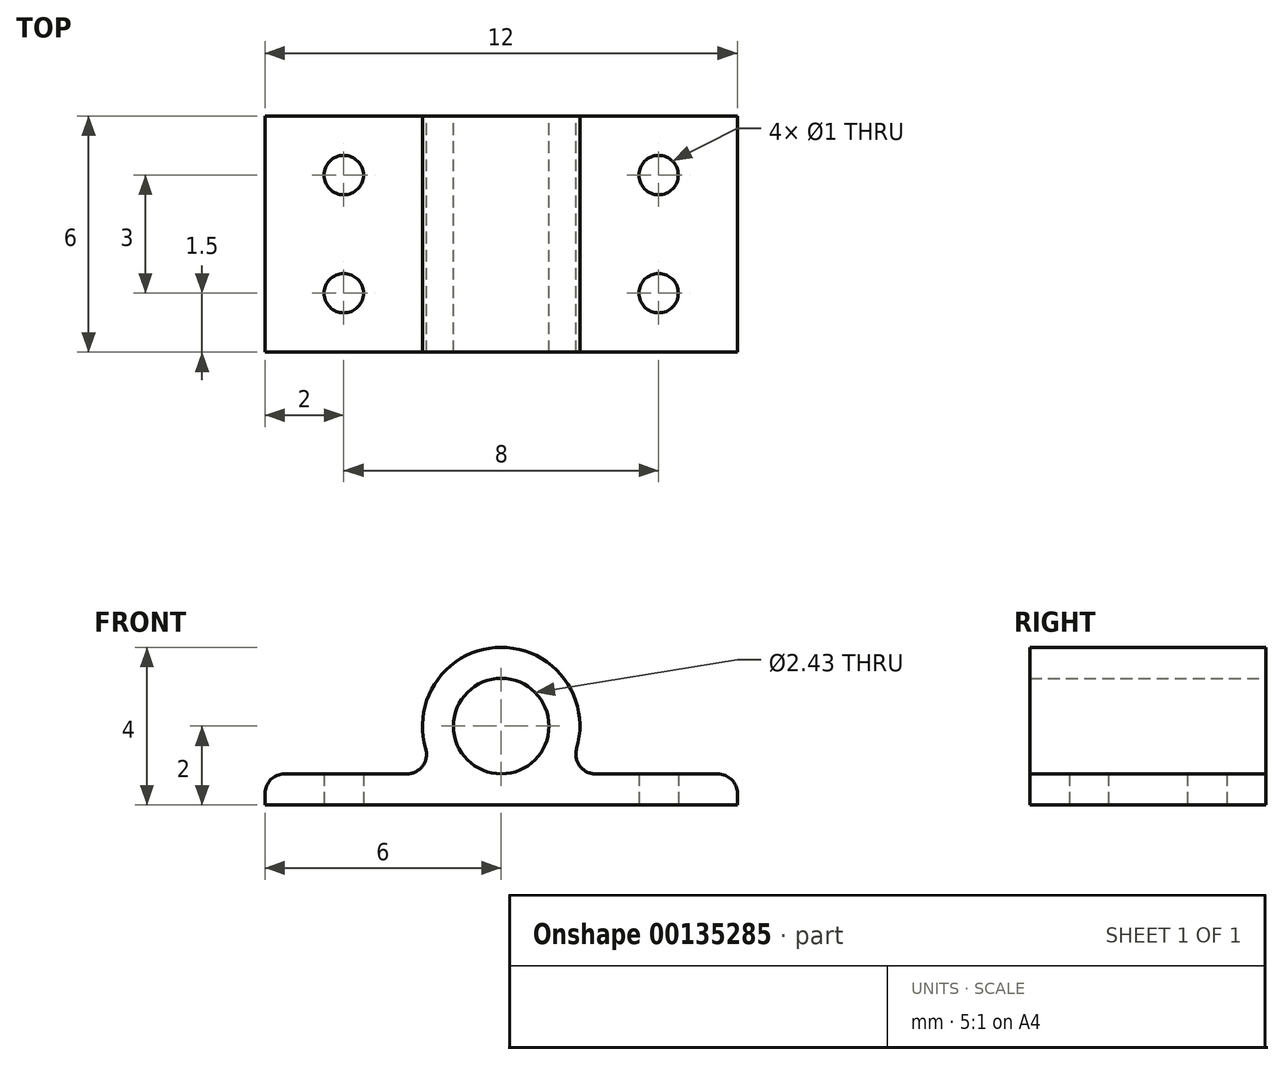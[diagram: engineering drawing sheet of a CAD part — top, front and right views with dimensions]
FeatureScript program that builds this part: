
annotation { "Feature Type Name" : "Feature", "Feature Type Description" : "" }
export const myFeature = defineFeature(function(context is Context, id is Id, definition is map)
    precondition{}
    {
        {
            var Q0;
            Q0=qCreatedBy(makeId("Front.planeOp"),FACE);
            var sketch = newSketch(context, id + "F0", { "sketchPlane" : qUnion([Q0])});
            skLineSegment(sketch, "E0.bottom", {"start": v(0, 0) * mm, "end": v(12, 0) * mm});
            skLineSegment(sketch, "E0.top", {"start": v(0, 0.79) * mm, "end": v(4.41, 0.79) * mm});
            skLineSegment(sketch, "E0.left", {"start": v(0, 0) * mm, "end": v(0, 0.79) * mm});
            skLineSegment(sketch, "E0.right", {"start": v(12, 0) * mm, "end": v(12, 0.79) * mm});
            skPoint(sketch, "E1.endSnap0", {"position": v(6, 0.79) * mm});
            skArc(sketch, "E2", {"start": v(7.59, 0.79) * mm, "mid": v(6, 4) * mm, "end": v(4.41, 0.79) * mm});
            skPoint(sketch, "E1.start.orphan", {"position": v(6, 0) * mm});
            skLineSegment(sketch, "E3.trimOffspring", {"start": v(7.59, 0.79) * mm, "end": v(12, 0.79) * mm});
            skCircle(sketch, "E4", {"center": v(6, 2) * mm, "radius": 1.21 * mm});
            skSolve(sketch);
        }
        {
            var Q0;
            Q0 = qSketchRegion(id + "F0", true);
            extrude(context, id + "F1", {"entities" : qUnion([Q0]), "depth" : 6 * mm});
        }
        {
            var Q0;
            Q0=makeQuery(id+"F1.opExtrude","SWEPT_FACE",FACE,{"disambiguationData":[OSD([sQuery(id+"F0.wireOp",EDGE,"E0.bottom")])]});
            var sketch = newSketch(context, id + "F2", { "sketchPlane" : qUnion([Q0])});
            skCircle(sketch, "E5", {"center": v(10, 1.5) * mm, "radius": 0.5 * mm});
            skCircle(sketch, "E6", {"center": v(2, 4.5) * mm, "radius": 0.5 * mm});
            skCircle(sketch, "E7", {"center": v(2, 1.5) * mm, "radius": 0.5 * mm});
            skCircle(sketch, "E8", {"center": v(10, 4.5) * mm, "radius": 0.5 * mm});
            skSolve(sketch);
        }
        {
            var Q0;
            Q0 = qSketchRegion(id + "F2", true);
            extrude(context, id + "F3", {"entities" : qUnion([Q0]), "operationType" : NewBodyOperationType.REMOVE, "oppositeDirection" : true, "depth" : 25 * mm});
        }
        {
            var Q0;
            Q0=makeQuery(id+"F1.opExtrude","SWEPT_EDGE",EDGE,{"disambiguationData":[OSD([sQuery(id+"F0.wireOp",EDGE,"E0.top"),sQuery(id+"F0.wireOp",EDGE,"E0.left")])]});
            var Q1;
            Q1=makeQuery(id+"F1.opExtrude","SWEPT_EDGE",EDGE,{"disambiguationData":[OSD([sQuery(id+"F0.wireOp",EDGE,"E0.right"),sQuery(id+"F0.wireOp",EDGE,"E3.trimOffspring")])]});
            var Q2;
            Q2=makeQuery(id+"F1.opExtrude","SWEPT_EDGE",EDGE,{"disambiguationData":[OSD([sQuery(id+"F0.wireOp",EDGE,"E2"),sQuery(id+"F0.wireOp",EDGE,"E3.trimOffspring")])]});
            var Q3;
            Q3=makeQuery(id+"F1.opExtrude","SWEPT_EDGE",EDGE,{"disambiguationData":[OSD([sQuery(id+"F0.wireOp",EDGE,"E0.top"),sQuery(id+"F0.wireOp",EDGE,"E2")])]});
            fillet(context, id + "F4", {"entities" : qUnion([Q0, Q1, Q2, Q3]), "radius" : 0.5 * mm, "tangentPropagation" : true, "allowEdgeOverflow" : false});
        }
    });
